# Revit family: R-MBD-331
name_source: partatom
category: Portes
units: mm (PartAtom-declared; Revit-internal decimal feet)

## family parameters
Couper avec des vides une fois chargée = Non
Hôte = Mur
Partagée = Non
Point de calcul de pièce = Oui
Toujours verticalement = Oui

## types (8) — shared parameters
1 Vantail = Non
2 Vantaux = Oui
A.E.V = non
Acoustique = non
Anti-Effraction = non
Coloris_Chants = BER
Coloris_Dormant = Hêtre
Coloris_Face_Cote_Oppose_Ouverture = Prépeint
Coloris_Face_Cote_Ouverture = Prépeint
Construction analytique = <Aucun>
DAS = Oui
DC Larg Feuillure = 12 mm  [stored 0.0393701 ft]
DC Pivot Vantail = 90 mm  [stored 0.295276 ft]
Description = Blocs-portes DAS résistants au feu - EI60 - Double action
Ep Profil Pose Tunnel = 118 mm
Ep Strat Vantail = 1 mm  [stored 0.00328084 ft]
Ep Vantail = 40 mm  [stored 0.131234 ft]
Epaisseur_Rainure à brique = 8 mm  [stored 0.0262467 ft]
Fabricant = MALERBA
Fiche_Produit = MBD-331
Fileur = Non
Jeu_Côté_Articulation_Vantail = 8 mm  [stored 0.0262467 ft]
Jeu_Côté_Fermeture_Vantail = 8 mm  [stored 0.0262467 ft]
Jeu_Haut = 2 mm  [stored 0.00656168 ft]
Larg Profil = 58 mm  [stored 0.190289 ft]
Larg Profil Avec Fileur = 20 mm  [stored 0.0656168 ft]
Larg Profil Trav = 68 mm
Largeur_Vantail_Service_Souhaitée = 930 mm  [stored 3.05118 ft]
Mat APD = Caoutchouc noir
Mat Parclose = BER 2
Mat Parclose Métal = Peinture Laquée PMT - Blanc Pur - RAL 9010
Materiaux_Dominant = Bois
Modèle = Va et vient
Montant_VV = Oui
Profondeur_Rainure à brique = 5 mm  [stored 0.0164042 ft]
Reference_Commerciale = 2V SP46/DA LINTEAU
Sans_Montants = Non
URL = https://www.malerba.fr
X_Axe Pivot = 114 mm  [stored 0.374016 ft]
X_DC seuil = 9 mm  [stored 0.0295276 ft]
zero-valued in all types: Jeu_1, Jeu_2, Largeur, Thermique (W/m2.°K), X_Inv_DC Larg Feuillure_1V Montant

## per-type parameters (varying)
| type | Hauteur_Tableau | Hauteur_Vantaux_Souhaitée | Largeur_Vantail_Semi_Fixe_Souhaitée |
| 2600x930x630 | 2680 mm  [stored 8.79265 ft] | 2600 mm  [stored 8.53018 ft] | 630 mm  [stored 2.06693 ft] |
| 2600x930x730 | 2680 mm  [stored 8.79265 ft] | 2600 mm  [stored 8.53018 ft] | 730 mm  [stored 2.39501 ft] |
| 2600x930x830 | 2680 mm  [stored 8.79265 ft] | 2600 mm  [stored 8.53018 ft] | 830 mm |
| 2600x930x930 | 2680 mm  [stored 8.79265 ft] | 2600 mm  [stored 8.53018 ft] | 930 mm  [stored 3.05118 ft] |
| 2040x930x730 | 2120 mm  [stored 6.95538 ft] | 2040 mm  [stored 6.69291 ft] | 730 mm  [stored 2.39501 ft] |
| 2040x930x830 | 2120 mm  [stored 6.95538 ft] | 2040 mm  [stored 6.69291 ft] | 830 mm |
| 2040x930x930 | 2120 mm  [stored 6.95538 ft] | 2040 mm  [stored 6.69291 ft] | 930 mm  [stored 3.05118 ft] |
| 2040x930x630 | 2120 mm  [stored 6.95538 ft] | 2040 mm  [stored 6.69291 ft] | 630 mm  [stored 2.06693 ft] |

note: [stored X ft] marks values corroborated as IEEE doubles in the binary element streams (Revit-internal decimal feet)

## geometry (parser evidence)
native form markers: Blend x12
no freeform markers — native parametric forms only
